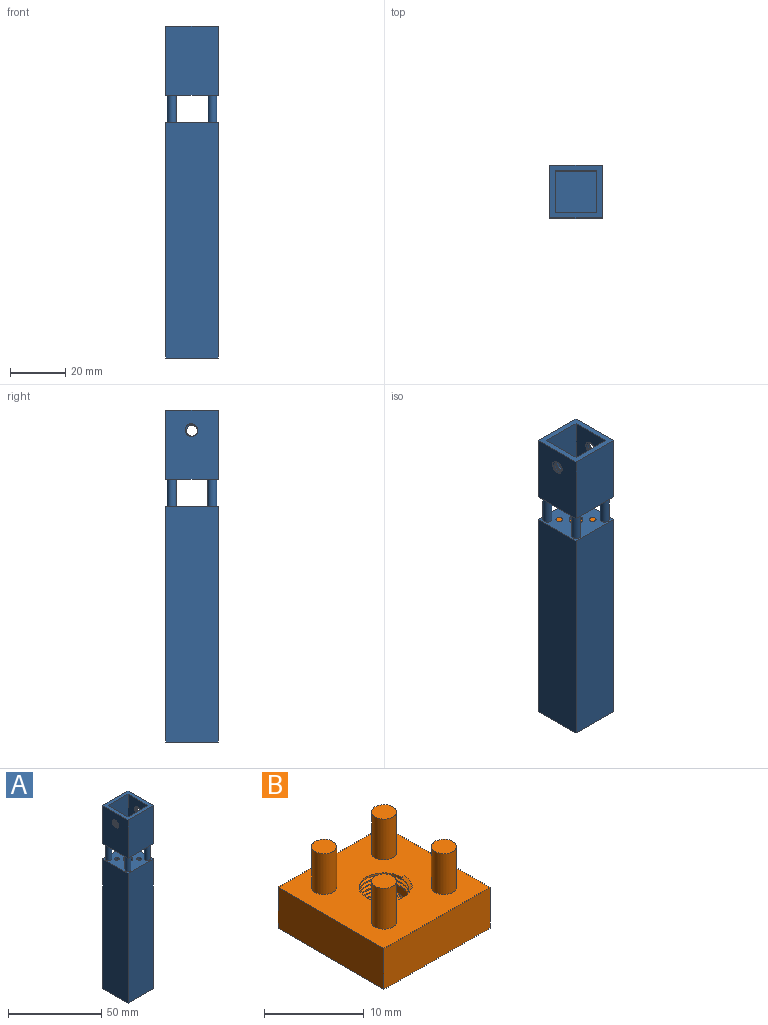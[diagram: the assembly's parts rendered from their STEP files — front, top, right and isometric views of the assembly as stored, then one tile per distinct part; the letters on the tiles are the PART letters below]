
ASSEMBLY  parts=2 mates=1
PART A: 43 faces, bbox 20.1x19.3x120.3 mm
  f0: plane 25.28x19.28mm, normal (-1,0,0), area 459.1mm2, adj f18,f19,f20,f25,f35,f36,f37,f38
  f1: plane 84.14x15.14mm, normal (-1,0,0), area 1256mm2, adj f2,f4,f10,f12,f39,f40,f41,f42
  f2: plane 84x15mm, normal (0,1,0), area 1260mm2, adj f1,f3,f10,f12
  f3: plane 84x15mm, normal (1,0,0), area 1260mm2, adj f2,f4,f10,f12
  f4: plane 84x15mm, normal (0,-1,0), area 1260mm2, adj f1,f3,f10,f12
  f5: plane 85x19mm, normal (0,-1,0), area 1615mm2, adj f6,f8,f9,f10
  f6: plane 85.14x19.14mm, normal (1,0,0), area 1611mm2, adj f5,f7,f9,f10,f39,f40,f41,f42
  f7: plane 85x19mm, normal (0,1,0), area 1615mm2, adj f6,f8,f9,f10
  f8: plane 85x19mm, normal (-1,0,0), area 1615mm2, adj f5,f7,f9,f10
  f9: plane 19x19mm, normal (0,0,1), area 289.3mm2, adj f5,f6,f7,f8,f11,f13,f14,f15
  f10: plane 19x19mm, normal (0,0,-1), area 136mm2, adj f1,f2,f3,f4,f5,f6,f7,f8
  f11: cylinder r=2.5mm len=5mm, axis (0,0,1), area 15.7mm2, adj f9,f12
  f12: plane 15x15mm, normal (0,0,-1), area 185.7mm2, adj f1,f2,f3,f4,f11,f27,f28,f29
  f13: cylinder r=1.61mm len=10mm, axis (0,0,-1), area 101mm2, adj f9,f20
  f14: cylinder r=1.61mm len=10mm, axis (0,0,-1), area 101mm2, adj f9,f20
  f15: cylinder r=1.61mm len=10mm, axis (0,0,-1), area 101mm2, adj f9,f20
  f16: cylinder r=1.61mm len=10mm, axis (0,0,-1), area 101mm2, adj f9,f20
  f17: plane 25.28x19.28mm, normal (1,0,0), area 459.1mm2, adj f18,f19,f20,f25,f31,f32,f33,f34
  f18: plane 25x19mm, normal (0,1,0), area 475mm2, adj f0,f17,f20,f25
  f19: plane 25x19mm, normal (0,-1,0), area 475mm2, adj f0,f17,f20,f25
  f20: plane 19x19mm, normal (0,0,-1), area 328.5mm2, adj f0,f13,f14,f15,f16,f17,f18,f19
  f21: plane 15x15mm, normal (0,1,0), area 225mm2, adj f22,f24,f25,f26
  f22: plane 15.28x15.28mm, normal (1,0,0), area 209.1mm2, adj f21,f23,f25,f26,f35,f36,f37,f38
  f23: plane 15x15mm, normal (0,-1,0), area 225mm2, adj f22,f24,f25,f26
  f24: plane 15.28x15.28mm, normal (-1,0,0), area 209.1mm2, adj f21,f23,f25,f26,f31,f32,f33,f34
  f25: plane 19x19mm, normal (0,0,1), area 136mm2, adj f0,f17,f18,f19,f21,f22,f23,f24
  f26: plane 15x15mm, normal (0,0,1), area 225mm2, adj f21,f22,f23,f24
  f27: cylinder r=1.25mm len=2.5mm, axis (0,0,1), area 7.9mm2, adj f9,f12
  f28: cylinder r=1.25mm len=2.5mm, axis (0,0,1), area 7.9mm2, adj f9,f12
  f29: cylinder r=1.25mm len=2.5mm, axis (0,0,1), area 7.9mm2, adj f9,f12
  f30: cylinder r=1.25mm len=2.5mm, axis (0,0,1), area 7.9mm2, adj f9,f12
  f31: bspline ~5.87x5.08mm, area 17.9mm2, adj f17,f24,f33,f34
  f32: bspline ~5.87x5.08mm, area 17.9mm2, adj f17,f24,f33,f34
  f33: bspline ~5.97x5.17mm, area 4.7mm2, adj f17,f24,f31,f32
  f34: cylinder r=2mm len=4mm, axis (-1,0,0), area 6.3mm2, adj f17,f24,f31,f32
  f35: bspline ~5.87x5.08mm, area 17.9mm2, adj f0,f22,f37,f38
  f36: bspline ~5.87x5.08mm, area 17.9mm2, adj f0,f22,f37,f38
  f37: bspline ~5.97x5.17mm, area 4.7mm2, adj f0,f22,f35,f36
  f38: cylinder r=2mm len=4mm, axis (-1,0,0), area 6.3mm2, adj f0,f22,f35,f36
  f39: bspline ~2.93x2.54mm, area 8.9mm2, adj f1,f6,f41,f42
  f40: bspline ~2.93x2.54mm, area 8.9mm2, adj f1,f6,f41,f42
  f41: bspline ~2.98x2.58mm, area 2.3mm2, adj f1,f6,f39,f40
  f42: cylinder r=1mm len=2mm, axis (-1,0,0), area 3.2mm2, adj f1,f6,f39,f40
PART B: 39 faces, bbox 15.4x15.2x10.4 mm
  f0: cylinder r=2.5mm len=5mm, axis (0,0,-1), area 8.6mm2, adj f10,f15,f23,f24,f25,f38
  f1: cylinder r=2.5mm len=5mm, axis (0,0,-1), area 8.3mm2, adj f5,f6,f11,f20,f22,f38
  f2: cylinder r=2.5mm len=5mm, axis (0,0,-1), area 2mm2, adj f7,f12,f38
  f3: cylinder r=2.5mm len=5mm, axis (0,0,-1), area 2mm2, adj f8,f13,f38
  f4: cylinder r=2.5mm len=5mm, axis (0,0,-1), area 2mm2, adj f9,f14,f38
  f5: bspline ~6.58x5.7mm, area 18.4mm2, adj f1,f11,f20,f38
  f6: bspline ~6.58x5.7mm, area 5.9mm2, adj f1,f12,f38
  f7: bspline ~6.58x5.7mm, area 5.6mm2, adj f2,f13,f38
  f8: bspline ~6.58x5.7mm, area 5.6mm2, adj f3,f14,f38
  f9: bspline ~6.58x5.7mm, area 5.8mm2, adj f4,f10,f38
  f10: bspline ~6.58x5.7mm, area 5.9mm2, adj f0,f9,f38
  f11: bspline ~6.58x5.7mm, area 19.4mm2, adj f1,f5,f22,f38
  f12: bspline ~6.58x5.7mm, area 5.8mm2, adj f2,f6,f38
  f13: bspline ~6.58x5.7mm, area 5.6mm2, adj f3,f7,f38
  f14: bspline ~6.58x5.7mm, area 5.6mm2, adj f4,f8,f38
  f15: plane 15.01x15.01mm, normal (0,0,1), area 184.7mm2, adj f0,f16,f17,f18,f19,f24,f25,f30
  f16: plane 15x5mm, normal (0,-1,0), area 75mm2, adj f15,f17,f19,f20
  f17: plane 15.2x5.2mm, normal (1,0,0), area 69.6mm2, adj f15,f16,f18,f20,f21,f26,f27
  f18: plane 15x5mm, normal (0,1,0), area 75mm2, adj f15,f17,f19,f20
  f19: plane 15x5mm, normal (-1,0,0), area 75mm2, adj f15,f16,f18,f20
  f20: plane 15.01x15.01mm, normal (0,0,-1), area 204.4mm2, adj f1,f5,f16,f17,f18,f19,f22
  f21: cylinder r=1.25mm len=4.5mm, axis (1,0,0), area 13.2mm2, adj f17,f26,f27,f28,f29,f38
  f22: plane 0.35x0.18mm, normal (0,1,0.03), area 0mm2, adj f1,f11,f20
  f23: bspline ~6.58x5.7mm, area 19.4mm2, adj f0,f24,f25,f38
  f24: plane 0.35x0.18mm, normal (0,-1,-0.03), area 0mm2, adj f0,f15,f23
  f25: bspline ~6.58x5.7mm, area 18.4mm2, adj f0,f15,f23,f38
  f26: bspline ~4.67x3.7mm, area 31mm2, adj f17,f21,f28,f29
  f27: plane 0.35x0.17mm, normal (-0.06,0,-1), area 0mm2, adj f17,f21,f29
  f28: plane 0.35x0.35mm, normal (0.06,0,1), area 0.1mm2, adj f21,f26,f29,f38
  f29: bspline ~4.67x3.2mm, area 31.7mm2, adj f21,f26,f27,f28,f38
  f30: cylinder r=1.25mm len=5mm, axis (0,0,-1), area 39.3mm2, adj f15,f31
  f31: plane 2.5x2.5mm, normal (0,0,1), area 4.9mm2, adj f30
  f32: cylinder r=1.25mm len=5mm, axis (0,0,-1), area 39.3mm2, adj f15,f33
  f33: plane 2.5x2.5mm, normal (0,0,1), area 4.9mm2, adj f32
  f34: cylinder r=1.25mm len=5mm, axis (0,0,-1), area 39.3mm2, adj f15,f35
  f35: plane 2.5x2.5mm, normal (0,0,1), area 4.9mm2, adj f34
  f36: cylinder r=1.25mm len=5mm, axis (0,0,-1), area 39.3mm2, adj f15,f37
  f37: plane 2.5x2.5mm, normal (0,0,1), area 4.9mm2, adj f36
  f38: extruded ~2.5x2.5mm, area 4.1mm2, adj f0,f1,f2,f3,f4,f5,f6,f7
PLACE A t=(-10.67,-4.87,-62.06)mm
PLACE B t=(-10.67,-4.88,-9.56)mm
MATE fastened B.f30 <-> A.f30  axis (0,0,1) through (-6.42,-0.64,-2.06)mm
